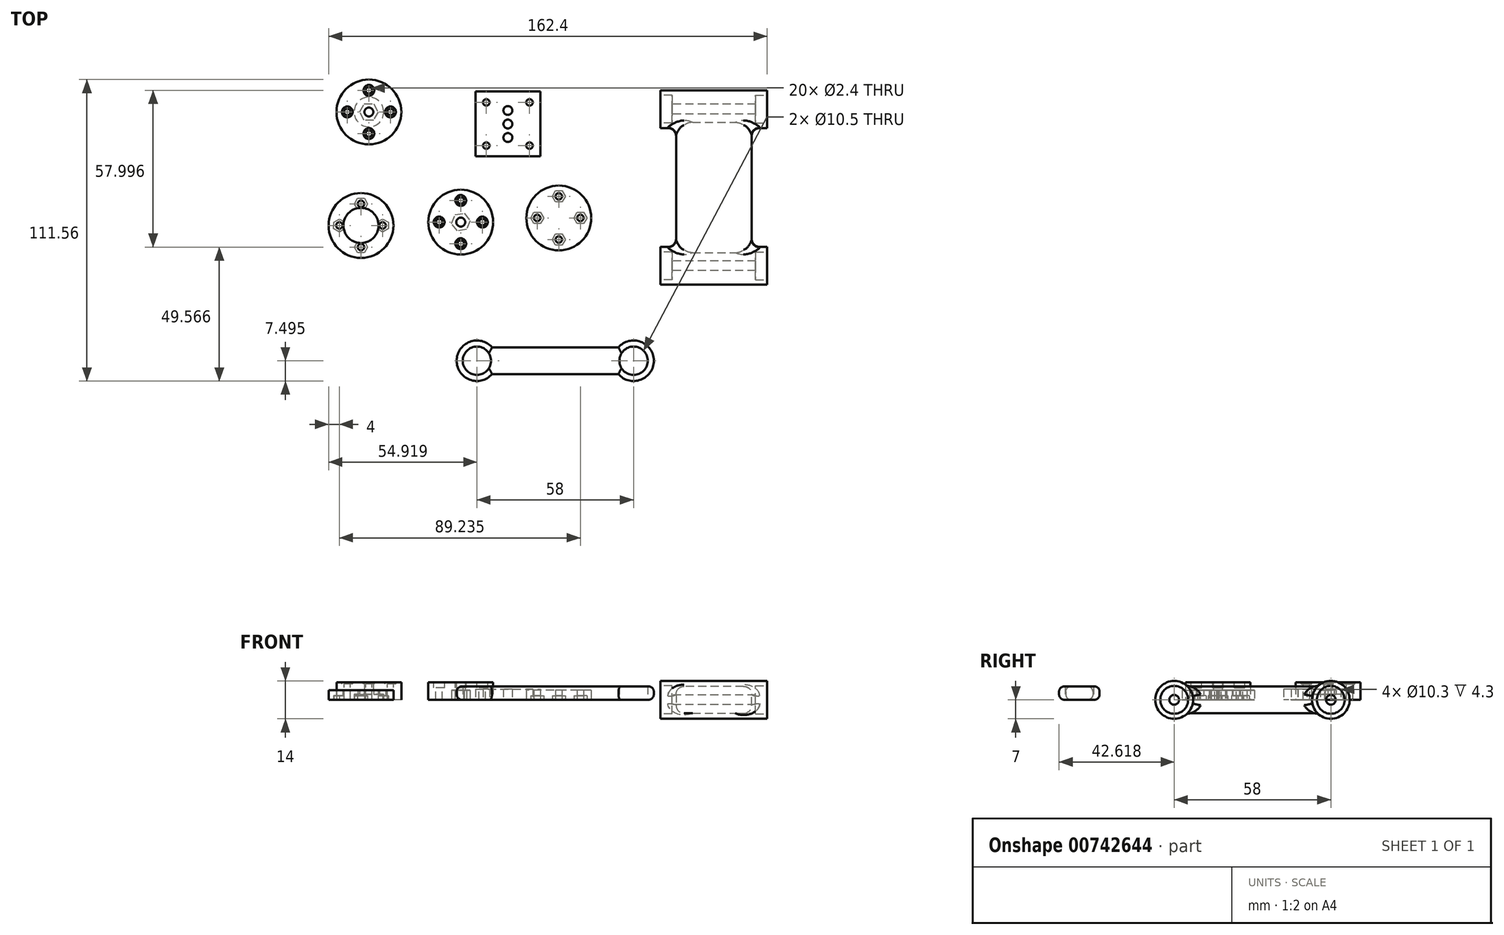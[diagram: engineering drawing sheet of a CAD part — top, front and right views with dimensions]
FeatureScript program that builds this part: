
annotation { "Feature Type Name" : "Feature", "Feature Type Description" : "" }
export const myFeature = defineFeature(function(context is Context, id is Id, definition is map)
    precondition{}
    {
        {
            var Q0;
            Q0=qCreatedBy(makeId("Top.planeOp"),FACE);
            var sketch = newSketch(context, id + "F0", { "sketchPlane" : qUnion([Q0])});
            skLineSegment(sketch, "E0.bottom", {"start": v(-51.58, 38.28) * mm, "end": v(-35.58, 38.28) * mm, "construction": true});
            skLineSegment(sketch, "E0.top", {"start": v(-51.58, 22.28) * mm, "end": v(-35.58, 22.28) * mm, "construction": true});
            skLineSegment(sketch, "E0.left", {"start": v(-51.58, 38.28) * mm, "end": v(-51.58, 22.28) * mm, "construction": true});
            skLineSegment(sketch, "E0.right", {"start": v(-35.58, 38.28) * mm, "end": v(-35.58, 22.28) * mm, "construction": true});
            skLineSegment(sketch, "E1.bottom", {"start": v(-55.58, 42.28) * mm, "end": v(-31.58, 42.28) * mm});
            skLineSegment(sketch, "E1.top", {"start": v(-55.58, 18.28) * mm, "end": v(-31.58, 18.28) * mm});
            skLineSegment(sketch, "E1.left", {"start": v(-55.58, 42.28) * mm, "end": v(-55.58, 18.28) * mm});
            skLineSegment(sketch, "E1.right", {"start": v(-31.58, 42.28) * mm, "end": v(-31.58, 18.28) * mm});
            skPoint(sketch, "E1.middle", {"position": v(-43.58, 30.28) * mm});
            skPoint(sketch, "E1.middle.positionSnap1", {"position": v(-35.58, 30.28) * mm});
            skPoint(sketch, "E1.centerSnap0", {"position": v(-43.58, 38.28) * mm});
            skPoint(sketch, "E1.centerSnap1", {"position": v(-35.58, 30.28) * mm});
            skPoint(sketch, "E2", {"position": v(-43.58, 22.28) * mm});
            skPoint(sketch, "E3", {"position": v(-43.58, 35.28) * mm});
            skPoint(sketch, "E4", {"position": v(-43.58, 25.28) * mm});
            skLineSegment(sketch, "E5", {"start": v(-43.58, 38.28) * mm, "end": v(-43.58, 35.28) * mm, "construction": true});
            skLineSegment(sketch, "E6", {"start": v(-43.58, 25.28) * mm, "end": v(-43.58, 22.28) * mm, "construction": true});
            skCircle(sketch, "E7", {"center": v(-35.58, 38.28) * mm, "radius": 0.75 * mm});
            skCircle(sketch, "E8", {"center": v(-51.58, 38.28) * mm, "radius": 0.75 * mm});
            skCircle(sketch, "E9", {"center": v(-51.58, 22.28) * mm, "radius": 0.75 * mm});
            skCircle(sketch, "E10", {"center": v(-35.58, 22.28) * mm, "radius": 0.75 * mm});
            skSolve(sketch);
        }
        {
            var Q0;
            Q0=makeQuery(id+"F0.imprint","IMPRINT",FACE,{"disambiguationData":[TD([[makeQuery(id+"F0.imprint","IMPRINT",EDGE,{"derivedFrom":sQuery(id+"F0.wireOp",EDGE,"E1.bottom")}),-1.0]])]});
            var Q1;
            Q1=makeQuery(id+"F0.imprint","IMPRINT",FACE,{"disambiguationData":[TD([[makeQuery(id+"F0.imprint","IMPRINT",EDGE,{"derivedFrom":sQuery(id+"F0.wireOp",EDGE,"E7")}),1.0]])]});
            var Q2;
            Q2=makeQuery(id+"F0.imprint","IMPRINT",FACE,{"disambiguationData":[TD([[makeQuery(id+"F0.imprint","IMPRINT",EDGE,{"derivedFrom":sQuery(id+"F0.wireOp",EDGE,"E8")}),1.0]])]});
            var Q3;
            Q3=makeQuery(id+"F0.imprint","IMPRINT",FACE,{"disambiguationData":[TD([[makeQuery(id+"F0.imprint","IMPRINT",EDGE,{"derivedFrom":sQuery(id+"F0.wireOp",EDGE,"E9")}),1.0]])]});
            var Q4;
            Q4=makeQuery(id+"F0.imprint","IMPRINT",FACE,{"disambiguationData":[TD([[makeQuery(id+"F0.imprint","IMPRINT",EDGE,{"derivedFrom":sQuery(id+"F0.wireOp",EDGE,"E10")}),1.0]])]});
            extrude(context, id + "F1", {"entities" : qUnion([Q0, Q1, Q2, Q3, Q4]), "depth" : 4 * mm, "offsetDistance" : 25 * mm});
        }
        {
            var Q0;
            Q0=sQuery(id+"F0.wireOp",VERTEX,"E1.middle.positionSnap0");
            var Q1;
            Q1=sQuery(id+"F0.wireOp",VERTEX,"455f30e0-36e8-462a-b0a7-f685abfa277a");
            var Q2;
            Q2=sQuery(id+"F0.wireOp",VERTEX,"E1.middle");
            var Q3;
            Q3=sQuery(id+"F0.wireOp",VERTEX,"a96c1f38-2630-4629-b729-bfcacf4a2e01");
            var Q4;
            Q4=sQuery(id+"F0.wireOp",VERTEX,"E3");
            var Q5;
            Q5=sQuery(id+"F0.wireOp",VERTEX,"E4");
            var Q6;
            Q6=makeQuery(id+"F1.opExtrude","SWEPT_BODY",BODY,{"disambiguationData":[OSD([sQuery(id+"F0.wireOp",EDGE,"E1.bottom"),sQuery(id+"F0.wireOp",EDGE,"E1.top"),sQuery(id+"F0.wireOp",EDGE,"E1.left"),sQuery(id+"F0.wireOp",EDGE,"E1.right")])]});
            hole(context, id + "F2", {"style" : HoleStyle.SIMPLE, "endStyle" : HoleEndStyle.BLIND, "oppositeDirection" : true, "holeDiameter" : 3.3 * mm, "majorDiameter" : 5 * mm, "holeDepth" : 12 * mm, "isTappedThrough" : true, "tappedDepth" : 10.5 * mm, "tapClearance" : 3, "locations" : qUnion([Q0, Q1, Q2, Q3, Q4, Q5]), "scope" : qUnion([Q6])});
        }
        {
            var Q0;
            Q0=sQuery(id+"F0.wireOp",VERTEX,"E0.top.start");
            var Q1;
            Q1=sQuery(id+"F0.wireOp",VERTEX,"E0.top.end");
            var Q2;
            Q2=sQuery(id+"F0.wireOp",VERTEX,"E0.bottom.end");
            var Q3;
            Q3=sQuery(id+"F0.wireOp",VERTEX,"E0.bottom.start");
            var Q4;
            Q4=makeQuery(id+"F1.opExtrude","SWEPT_BODY",BODY,{"disambiguationData":[OSD([sQuery(id+"F0.wireOp",EDGE,"E1.bottom"),sQuery(id+"F0.wireOp",EDGE,"E1.top"),sQuery(id+"F0.wireOp",EDGE,"E1.left"),sQuery(id+"F0.wireOp",EDGE,"E1.right")])]});
            hole(context, id + "F3", {"style" : HoleStyle.SIMPLE, "endStyle" : HoleEndStyle.BLIND, "oppositeDirection" : true, "holeDiameter" : 2.4 * mm, "majorDiameter" : 5 * mm, "holeDepth" : 30 * mm, "isTappedThrough" : true, "tappedDepth" : 10.5 * mm, "tapClearance" : 3, "locations" : qUnion([Q0, Q1, Q2, Q3]), "scope" : qUnion([Q4])});
        }
        {
            var Q0;
            Q0=qCreatedBy(makeId("Top.planeOp"),FACE);
            var sketch = newSketch(context, id + "F4", { "sketchPlane" : qUnion([Q0])});
            skLineSegment(sketch, "E11", {"start": v(12.93, 35.79) * mm, "end": v(52.43, 35.79) * mm});
            skLineSegment(sketch, "E12", {"start": v(32.68, 35.79) * mm, "end": v(32.68, -22.21) * mm});
            skLineSegment(sketch, "E13", {"start": v(13, -22.21) * mm, "end": v(52.5, -22.21) * mm});
            skSolve(sketch);
        }
        {
            var Q0;
            Q0=qCreatedBy(makeId("Right.planeOp"),FACE);
            var Q1;
            Q1=sQuery(id+"F4.wireOp",VERTEX,"E11.start");
            cPlane(context, id + "F5", {"entities" : qUnion([Q0, Q1]), "cplaneType" : CPlaneType.PLANE_POINT, "offset" : 25 * mm, "width" : 150 * mm, "height" : 150 * mm});
        }
        {
            var Q0;
            Q0=qCreatedBy(id+"F5.planeOp",FACE);
            var sketch = newSketch(context, id + "F6", { "sketchPlane" : qUnion([Q0])});
            skCircle(sketch, "E14", {"center": v(35.79, 0) * mm, "radius": 7 * mm});
            skCircle(sketch, "E15", {"center": v(-22.21, 0) * mm, "radius": 7 * mm});
            skCircle(sketch, "E16", {"center": v(35.79, 0) * mm, "radius": 5.15 * mm});
            skCircle(sketch, "E17", {"center": v(-22.21, 0) * mm, "radius": 5.15 * mm});
            skSolve(sketch);
        }
        {
            var Q0;
            Q0=sQuery(id+"F4.wireOp",EDGE,"E13");
            cPoint(context, id + "F7", {"entities" : qUnion([Q0]), "parameter" : 0.5});
        }
        {
            var Q0;
            Q0=qCreatedBy(makeId("Front.planeOp"),FACE);
            var Q1;
            Q1 = qCreatedBy(id + "F7" ,VERTEX);
            cPlane(context, id + "F8", {"entities" : qUnion([Q0, Q1]), "cplaneType" : CPlaneType.PLANE_POINT, "offset" : 25 * mm, "width" : 150 * mm, "height" : 150 * mm});
        }
        {
            var Q0;
            Q0=qCreatedBy(id+"F8.planeOp",FACE);
            var sketch = newSketch(context, id + "F9", { "sketchPlane" : qUnion([Q0])});
            skLineSegment(sketch, "E18.bottom", {"start": v(46.68, 5) * mm, "end": v(18.68, 5) * mm});
            skLineSegment(sketch, "E18.top", {"start": v(46.68, -5) * mm, "end": v(18.68, -5) * mm});
            skLineSegment(sketch, "E18.left", {"start": v(46.68, 5) * mm, "end": v(46.68, -5) * mm});
            skLineSegment(sketch, "E18.right", {"start": v(18.68, 5) * mm, "end": v(18.68, -5) * mm});
            skPoint(sketch, "E18.middle", {"position": v(32.68, 0) * mm});
            skSolve(sketch);
        }
        {
            var Q0;
            Q0=makeQuery(id+"F6.imprint","IMPRINT",FACE,{"disambiguationData":[TD([[makeQuery(id+"F6.imprint","IMPRINT",EDGE,{"derivedFrom":sQuery(id+"F6.wireOp",EDGE,"E14")}),1.0]])]});
            var Q1;
            Q1=makeQuery(id+"F6.imprint","IMPRINT",FACE,{"disambiguationData":[TD([[makeQuery(id+"F6.imprint","IMPRINT",EDGE,{"derivedFrom":sQuery(id+"F6.wireOp",EDGE,"E15")}),1.0]])]});
            var Q2;
            Q2=makeQuery(id+"F6.imprint","IMPRINT",FACE,{"disambiguationData":[TD([[makeQuery(id+"F6.imprint","IMPRINT",EDGE,{"derivedFrom":sQuery(id+"F6.wireOp",EDGE,"E16")}),1.0]])]});
            var Q3;
            Q3=makeQuery(id+"F6.imprint","IMPRINT",FACE,{"disambiguationData":[TD([[makeQuery(id+"F6.imprint","IMPRINT",EDGE,{"derivedFrom":sQuery(id+"F6.wireOp",EDGE,"E17")}),1.0]])]});
            var Q4;
            Q4=sQuery(id+"F6.wireOp",EDGE,"E14");
            var Q5;
            Q5=sQuery(id+"F6.wireOp",EDGE,"E15");
            var Q6;
            Q6=sQuery(id+"F4.wireOp",EDGE,"E11");
            sweep(context, id + "F10", {"profiles" : qUnion([Q0, Q1, Q2, Q3]), "surfaceProfiles" : qUnion([Q4, Q5]), "path" : qUnion([Q6])});
        }
        {
            var Q0;
            Q0=makeQuery(id+"F9.imprint","IMPRINT",FACE,{"disambiguationData":[TD([[makeQuery(id+"F9.imprint","IMPRINT",EDGE,{"derivedFrom":sQuery(id+"F9.wireOp",EDGE,"E18.bottom")}),1.0]])]});
            var Q1;
            Q1=sQuery(id+"F4.wireOp",EDGE,"E12");
            sweep(context, id + "F11", {"operationType" : NewBodyOperationType.ADD, "profiles" : qUnion([Q0]), "path" : qUnion([Q1])});
        }
        {
            var Q0;
            Q0=makeQuery(id+"F11.opSweep","SWEPT_FACE",FACE,{"disambiguationData":[OSD([sQuery(id+"F4.wireOp",EDGE,"E12"),sQuery(id+"F9.wireOp",EDGE,"E18.right")])]});
            var Q1;
            Q1=makeQuery(id+"F11.opSweep","SWEPT_FACE",FACE,{"disambiguationData":[OSD([sQuery(id+"F4.wireOp",EDGE,"E12"),sQuery(id+"F9.wireOp",EDGE,"E18.left")])]});
            var Q2;
            Q2=makeQuery(id+"F11.opSweep","SWEPT_FACE",FACE,{"disambiguationData":[OSD([sQuery(id+"F4.wireOp",EDGE,"E12"),sQuery(id+"F9.wireOp",EDGE,"E18.bottom")])]});
            fillet(context, id + "F12", {"entities" : qUnion([Q0, Q1, Q2]), "radius" : 3 * mm, "tangentPropagation" : true, "allowEdgeOverflow" : false});
        }
        {
            var Q0;
            Q0=sQuery(id+"F6.wireOp",VERTEX,"E14.center");
            var Q1;
            Q1=sQuery(id+"F6.wireOp",VERTEX,"E15.center");
            var Q2;
            Q2=makeQuery(id+"F10.opSweep","SWEPT_BODY",BODY,{"disambiguationData":[OSD([sQuery(id+"F4.wireOp",EDGE,"E11"),sQuery(id+"F6.wireOp",EDGE,"E14")])]});
            hole(context, id + "F13", {"style" : HoleStyle.SIMPLE, "endStyle" : HoleEndStyle.THROUGH, "oppositeDirection" : true, "holeDiameter" : 3.6 * mm, "majorDiameter" : 5 * mm, "isTappedThrough" : true, "tappedDepth" : 10.5 * mm, "tapClearance" : 3, "locations" : qUnion([Q0, Q1]), "scope" : qUnion([Q2])});
        }
        {
            var Q0;
            Q0=makeQuery(id+"F10.opSweep","CAP_FACE",FACE,{"disambiguationData":[OSD([sQuery(id+"F4.wireOp",VERTEX,"E11.end"),sQuery(id+"F6.wireOp",EDGE,"E14")])],"isStart":false});
            var sketch = newSketch(context, id + "F14", { "sketchPlane" : qUnion([Q0])});
            skCircle(sketch, "E19", {"center": v(-22.21, 0) * mm, "radius": 5.15 * mm});
            skCircle(sketch, "E20", {"center": v(35.79, 0) * mm, "radius": 5.15 * mm});
            skSolve(sketch);
        }
        {
            var Q0;
            Q0=makeQuery(id+"F14.imprint","IMPRINT",FACE,{"disambiguationData":[TD([[makeQuery(id+"F14.imprint","IMPRINT",EDGE,{"derivedFrom":sQuery(id+"F14.wireOp",EDGE,"E19")}),1.0]])]});
            var Q1;
            Q1=makeQuery(id+"F6.imprint","IMPRINT",FACE,{"disambiguationData":[TD([[makeQuery(id+"F6.imprint","IMPRINT",EDGE,{"derivedFrom":sQuery(id+"F6.wireOp",EDGE,"E17")}),1.0]])]});
            var Q2;
            Q2=makeQuery(id+"F14.imprint","IMPRINT",FACE,{"disambiguationData":[TD([[makeQuery(id+"F14.imprint","IMPRINT",EDGE,{"derivedFrom":sQuery(id+"F14.wireOp",EDGE,"E20")}),1.0]])]});
            extrude(context, id + "F15", {"entities" : qUnion([Q0, Q1, Q2]), "operationType" : NewBodyOperationType.REMOVE, "oppositeDirection" : true, "depth" : 4.3 * mm, "offsetDistance" : 25 * mm});
        }
        {
            var Q0;
            Q0=makeQuery(id+"F6.imprint","IMPRINT",FACE,{"disambiguationData":[TD([[makeQuery(id+"F6.imprint","IMPRINT",EDGE,{"derivedFrom":sQuery(id+"F6.wireOp",EDGE,"E17")}),1.0]])]});
            var Q1;
            Q1=makeQuery(id+"F6.imprint","IMPRINT",FACE,{"disambiguationData":[TD([[makeQuery(id+"F6.imprint","IMPRINT",EDGE,{"derivedFrom":sQuery(id+"F6.wireOp",EDGE,"E16")}),1.0]])]});
            extrude(context, id + "F16", {"entities" : qUnion([Q0, Q1]), "operationType" : NewBodyOperationType.REMOVE, "depth" : 4.3 * mm, "offsetDistance" : 25 * mm});
        }
        {
            var Q0;
            Q0=qCreatedBy(makeId("Top.planeOp"),FACE);
            var sketch = newSketch(context, id + "F17", { "sketchPlane" : qUnion([Q0])});
            skCircle(sketch, "E21", {"center": v(-61.03, -6.02) * mm, "radius": 8 * mm, "construction": true});
            skCircle(sketch, "E22", {"center": v(-61.03, -6.02) * mm, "radius": 12 * mm});
            skPoint(sketch, "E23", {"position": v(-61.03, 1.98) * mm});
            skPoint(sketch, "E24", {"position": v(-61.03, -14.02) * mm});
            skPoint(sketch, "E25", {"position": v(-53.03, -6.02) * mm});
            skPoint(sketch, "E26", {"position": v(-69.03, -6.02) * mm});
            skCircle(sketch, "E27.cCircle", {"center": v(-61.03, -6.02) * mm, "radius": 3 * mm, "construction": true});
            skLineSegment(sketch, "E27.0", {"start": v(-59.75, -2.8) * mm, "end": v(-57.6, -5.52) * mm});
            skLineSegment(sketch, "E27.1", {"start": v(-57.6, -5.52) * mm, "end": v(-58.89, -8.74) * mm});
            skLineSegment(sketch, "E27.2", {"start": v(-58.89, -8.74) * mm, "end": v(-62.32, -9.24) * mm});
            skLineSegment(sketch, "E27.3", {"start": v(-62.32, -9.24) * mm, "end": v(-64.46, -6.52) * mm});
            skLineSegment(sketch, "E27.4", {"start": v(-64.46, -6.52) * mm, "end": v(-63.18, -3.3) * mm});
            skLineSegment(sketch, "E27.5", {"start": v(-63.18, -3.3) * mm, "end": v(-59.75, -2.8) * mm});
            skPoint(sketch, "E27.0.midPoint", {"position": v(-58.68, -4.16) * mm});
            skCircle(sketch, "E28", {"center": v(-24.74, -4.5) * mm, "radius": 8 * mm, "construction": true});
            skCircle(sketch, "E29", {"center": v(-24.74, -4.5) * mm, "radius": 12 * mm});
            skPoint(sketch, "E30", {"position": v(-24.74, -12.5) * mm});
            skPoint(sketch, "E31", {"position": v(-16.74, -4.5) * mm});
            skPoint(sketch, "E32", {"position": v(-32.74, -4.5) * mm});
            skPoint(sketch, "E33", {"position": v(-24.74, 3.5) * mm});
            skCircle(sketch, "E34.cCircle", {"center": v(-24.74, 3.5) * mm, "radius": 2.1 * mm, "construction": true});
            skLineSegment(sketch, "E34.0", {"start": v(-23.52, 5.6) * mm, "end": v(-22.31, 3.5) * mm});
            skLineSegment(sketch, "E34.1", {"start": v(-22.31, 3.5) * mm, "end": v(-23.52, 1.4) * mm});
            skLineSegment(sketch, "E34.2", {"start": v(-23.52, 1.4) * mm, "end": v(-25.95, 1.4) * mm});
            skLineSegment(sketch, "E34.3", {"start": v(-25.95, 1.4) * mm, "end": v(-27.16, 3.5) * mm});
            skLineSegment(sketch, "E34.4", {"start": v(-27.16, 3.5) * mm, "end": v(-25.95, 5.6) * mm});
            skLineSegment(sketch, "E34.5", {"start": v(-25.95, 5.6) * mm, "end": v(-23.52, 5.6) * mm});
            skPoint(sketch, "E34.0.midPoint", {"position": v(-22.92, 4.56) * mm});
            skCircle(sketch, "E35.cCircle", {"center": v(-16.74, -4.5) * mm, "radius": 2.1 * mm, "construction": true});
            skLineSegment(sketch, "E35.0", {"start": v(-17.95, -2.4) * mm, "end": v(-15.52, -2.4) * mm});
            skLineSegment(sketch, "E35.1", {"start": v(-15.52, -2.4) * mm, "end": v(-14.31, -4.5) * mm});
            skLineSegment(sketch, "E35.2", {"start": v(-14.31, -4.5) * mm, "end": v(-15.52, -6.6) * mm});
            skLineSegment(sketch, "E35.3", {"start": v(-15.52, -6.6) * mm, "end": v(-17.95, -6.6) * mm});
            skLineSegment(sketch, "E35.4", {"start": v(-17.95, -6.6) * mm, "end": v(-19.16, -4.5) * mm});
            skLineSegment(sketch, "E35.5", {"start": v(-19.16, -4.5) * mm, "end": v(-17.95, -2.4) * mm});
            skPoint(sketch, "E35.0.midPoint", {"position": v(-16.74, -2.4) * mm});
            skCircle(sketch, "E36.cCircle", {"center": v(-24.74, -12.5) * mm, "radius": 2.1 * mm, "construction": true});
            skLineSegment(sketch, "E36.0", {"start": v(-23.52, -10.4) * mm, "end": v(-22.31, -12.5) * mm});
            skLineSegment(sketch, "E36.1", {"start": v(-22.31, -12.5) * mm, "end": v(-23.52, -14.6) * mm});
            skLineSegment(sketch, "E36.2", {"start": v(-23.52, -14.6) * mm, "end": v(-25.95, -14.6) * mm});
            skLineSegment(sketch, "E36.3", {"start": v(-25.95, -14.6) * mm, "end": v(-27.16, -12.5) * mm});
            skLineSegment(sketch, "E36.4", {"start": v(-27.16, -12.5) * mm, "end": v(-25.95, -10.4) * mm});
            skLineSegment(sketch, "E36.5", {"start": v(-25.95, -10.4) * mm, "end": v(-23.52, -10.4) * mm});
            skPoint(sketch, "E36.0.midPoint", {"position": v(-22.92, -11.44) * mm});
            skCircle(sketch, "E37.cCircle", {"center": v(-32.74, -4.5) * mm, "radius": 2.1 * mm, "construction": true});
            skLineSegment(sketch, "E37.0", {"start": v(-31.52, -2.4) * mm, "end": v(-30.31, -4.5) * mm});
            skLineSegment(sketch, "E37.1", {"start": v(-30.31, -4.5) * mm, "end": v(-31.52, -6.6) * mm});
            skLineSegment(sketch, "E37.2", {"start": v(-31.52, -6.6) * mm, "end": v(-33.95, -6.6) * mm});
            skLineSegment(sketch, "E37.3", {"start": v(-33.95, -6.6) * mm, "end": v(-35.16, -4.5) * mm});
            skLineSegment(sketch, "E37.4", {"start": v(-35.16, -4.5) * mm, "end": v(-33.95, -2.4) * mm});
            skLineSegment(sketch, "E37.5", {"start": v(-33.95, -2.4) * mm, "end": v(-31.52, -2.4) * mm});
            skPoint(sketch, "E37.0.midPoint", {"position": v(-30.92, -3.44) * mm});
            skLineSegment(sketch, "E38", {"start": v(-36.74, -4.5) * mm, "end": v(-12.74, -4.5) * mm, "construction": true});
            skLineSegment(sketch, "E39", {"start": v(-24.74, 7.5) * mm, "end": v(-24.74, -16.5) * mm, "construction": true});
            skPoint(sketch, "E40", {"position": v(-24.74, 5.6) * mm});
            skPoint(sketch, "E41", {"position": v(-24.74, -10.4) * mm});
            skCircle(sketch, "E42", {"center": v(-55.05, -57.33) * mm, "radius": 5.25 * mm});
            skCircle(sketch, "E43", {"center": v(-55.05, -57.33) * mm, "radius": 7.5 * mm});
            skLineSegment(sketch, "E44", {"start": v(-55.05, -57.33) * mm, "end": v(2.95, -57.33) * mm});
            skCircle(sketch, "E45", {"center": v(2.95, -57.33) * mm, "radius": 5.25 * mm});
            skCircle(sketch, "E46", {"center": v(2.95, -57.33) * mm, "radius": 7.5 * mm});
            skPoint(sketch, "E47", {"position": v(-26.05, -57.33) * mm});
            skLineSegment(sketch, "E48.bottom", {"start": v(-49.46, -52.33) * mm, "end": v(-2.64, -52.33) * mm});
            skLineSegment(sketch, "E48.top", {"start": v(-49.46, -62.33) * mm, "end": v(-2.64, -62.33) * mm});
            skLineSegment(sketch, "E48.left", {"start": v(-49.46, -52.33) * mm, "end": v(-49.46, -62.33) * mm});
            skLineSegment(sketch, "E48.right", {"start": v(-2.64, -52.33) * mm, "end": v(-2.64, -62.33) * mm});
            skCircle(sketch, "E49", {"center": v(-97.97, -7.26) * mm, "radius": 8 * mm, "construction": true});
            skCircle(sketch, "E50", {"center": v(-97.97, -7.26) * mm, "radius": 12 * mm});
            skPoint(sketch, "E51", {"position": v(-97.97, -15.26) * mm});
            skPoint(sketch, "E52", {"position": v(-89.97, -7.26) * mm});
            skPoint(sketch, "E53", {"position": v(-105.97, -7.26) * mm});
            skPoint(sketch, "E54", {"position": v(-97.97, 0.74) * mm});
            skCircle(sketch, "E55.cCircle", {"center": v(-97.97, 0.74) * mm, "radius": 2.1 * mm, "construction": true});
            skLineSegment(sketch, "E55.0", {"start": v(-96.76, 2.84) * mm, "end": v(-95.55, 0.74) * mm});
            skLineSegment(sketch, "E55.1", {"start": v(-95.55, 0.74) * mm, "end": v(-96.76, -1.36) * mm});
            skLineSegment(sketch, "E55.2", {"start": v(-96.76, -1.36) * mm, "end": v(-99.18, -1.36) * mm});
            skLineSegment(sketch, "E55.3", {"start": v(-99.18, -1.36) * mm, "end": v(-100.4, 0.74) * mm});
            skLineSegment(sketch, "E55.4", {"start": v(-100.4, 0.74) * mm, "end": v(-99.18, 2.84) * mm});
            skLineSegment(sketch, "E55.5", {"start": v(-99.18, 2.84) * mm, "end": v(-96.76, 2.84) * mm});
            skPoint(sketch, "E55.0.midPoint", {"position": v(-96.15, 1.79) * mm});
            skCircle(sketch, "E56.cCircle", {"center": v(-97.97, -15.26) * mm, "radius": 2.1 * mm, "construction": true});
            skLineSegment(sketch, "E56.0", {"start": v(-96.76, -13.16) * mm, "end": v(-95.55, -15.26) * mm});
            skLineSegment(sketch, "E56.1", {"start": v(-95.55, -15.26) * mm, "end": v(-96.76, -17.36) * mm});
            skLineSegment(sketch, "E56.2", {"start": v(-96.76, -17.36) * mm, "end": v(-99.18, -17.36) * mm});
            skLineSegment(sketch, "E56.3", {"start": v(-99.18, -17.36) * mm, "end": v(-100.4, -15.26) * mm});
            skLineSegment(sketch, "E56.4", {"start": v(-100.4, -15.26) * mm, "end": v(-99.18, -13.16) * mm});
            skLineSegment(sketch, "E56.5", {"start": v(-99.18, -13.16) * mm, "end": v(-96.76, -13.16) * mm});
            skPoint(sketch, "E56.0.midPoint", {"position": v(-96.15, -14.21) * mm});
            skLineSegment(sketch, "E57", {"start": v(-109.97, -7.26) * mm, "end": v(-85.97, -7.26) * mm, "construction": true});
            skLineSegment(sketch, "E58", {"start": v(-97.97, 4.74) * mm, "end": v(-97.97, -19.26) * mm, "construction": true});
            skPoint(sketch, "E59", {"position": v(-97.97, 2.84) * mm});
            skPoint(sketch, "E60", {"position": v(-97.97, -13.16) * mm});
            skCircle(sketch, "E61", {"center": v(-97.97, -7.26) * mm, "radius": 6.5 * mm});
            skLineSegment(sketch, "E62", {"start": v(-89.97, 0.12) * mm, "end": v(-89.97, -14.94) * mm, "construction": true});
            skLineSegment(sketch, "E63", {"start": v(-105.97, -0.94) * mm, "end": v(-105.97, -14.47) * mm, "construction": true});
            skCircle(sketch, "E64.cCircle", {"center": v(-105.97, -7.26) * mm, "radius": 2.1 * mm, "construction": true});
            skLineSegment(sketch, "E64.0", {"start": v(-108.05, -6.02) * mm, "end": v(-105.94, -4.84) * mm});
            skLineSegment(sketch, "E64.1", {"start": v(-105.94, -4.84) * mm, "end": v(-103.85, -6.08) * mm});
            skLineSegment(sketch, "E64.2", {"start": v(-103.85, -6.08) * mm, "end": v(-103.89, -8.5) * mm});
            skLineSegment(sketch, "E64.3", {"start": v(-103.89, -8.5) * mm, "end": v(-106, -9.69) * mm});
            skLineSegment(sketch, "E64.4", {"start": v(-106, -9.69) * mm, "end": v(-108.09, -8.45) * mm});
            skLineSegment(sketch, "E64.5", {"start": v(-108.09, -8.45) * mm, "end": v(-108.05, -6.02) * mm});
            skPoint(sketch, "E64.0.midPoint", {"position": v(-107, -5.43) * mm});
            skCircle(sketch, "E65.cCircle", {"center": v(-89.97, -7.26) * mm, "radius": 2.1 * mm, "construction": true});
            skLineSegment(sketch, "E65.0", {"start": v(-89.97, -4.84) * mm, "end": v(-87.87, -6.05) * mm});
            skLineSegment(sketch, "E65.1", {"start": v(-87.87, -6.05) * mm, "end": v(-87.87, -8.48) * mm});
            skLineSegment(sketch, "E65.2", {"start": v(-87.87, -8.48) * mm, "end": v(-89.97, -9.69) * mm});
            skLineSegment(sketch, "E65.3", {"start": v(-89.97, -9.69) * mm, "end": v(-92.07, -8.48) * mm});
            skLineSegment(sketch, "E65.4", {"start": v(-92.07, -8.48) * mm, "end": v(-92.07, -6.05) * mm});
            skLineSegment(sketch, "E65.5", {"start": v(-92.07, -6.05) * mm, "end": v(-89.97, -4.84) * mm});
            skPoint(sketch, "E65.0.midPoint", {"position": v(-88.92, -5.45) * mm});
            skCircle(sketch, "E66", {"center": v(-95.05, 34.73) * mm, "radius": 8 * mm, "construction": true});
            skCircle(sketch, "E67", {"center": v(-95.05, 34.73) * mm, "radius": 12 * mm});
            skPoint(sketch, "E68", {"position": v(-95.05, 42.73) * mm});
            skPoint(sketch, "E69", {"position": v(-95.05, 26.73) * mm});
            skPoint(sketch, "E70", {"position": v(-87.05, 34.73) * mm});
            skPoint(sketch, "E71", {"position": v(-103.05, 34.73) * mm});
            skCircle(sketch, "E72.cCircle", {"center": v(-95.05, 34.73) * mm, "radius": 3 * mm, "construction": true});
            skLineSegment(sketch, "E72.0", {"start": v(-93.32, 37.73) * mm, "end": v(-91.59, 34.73) * mm});
            skLineSegment(sketch, "E72.1", {"start": v(-91.59, 34.73) * mm, "end": v(-93.32, 31.73) * mm});
            skLineSegment(sketch, "E72.2", {"start": v(-93.32, 31.73) * mm, "end": v(-96.78, 31.73) * mm});
            skLineSegment(sketch, "E72.3", {"start": v(-96.78, 31.73) * mm, "end": v(-98.51, 34.73) * mm});
            skLineSegment(sketch, "E72.4", {"start": v(-98.51, 34.73) * mm, "end": v(-96.78, 37.73) * mm});
            skLineSegment(sketch, "E72.5", {"start": v(-96.78, 37.73) * mm, "end": v(-93.32, 37.73) * mm});
            skPoint(sketch, "E72.0.midPoint", {"position": v(-92.45, 36.23) * mm});
            skCircle(sketch, "E73", {"center": v(-95.05, 34.73) * mm, "radius": 5.5 * mm});
            skLineSegment(sketch, "E74", {"start": v(-95.05, 46.73) * mm, "end": v(-95.05, 22.73) * mm, "construction": true});
            skLineSegment(sketch, "E75", {"start": v(-107.05, 34.73) * mm, "end": v(-83.05, 34.73) * mm, "construction": true});
            skSolve(sketch);
        }
        {
            var Q0;
            Q0=makeQuery(id+"F17.imprint","IMPRINT",FACE,{"disambiguationData":[TD([[makeQuery(id+"F17.imprint","IMPRINT",EDGE,{"derivedFrom":sQuery(id+"F17.wireOp",EDGE,"E22")}),1.0]])]});
            var Q1;
            Q1=makeQuery(id+"F17.imprint","IMPRINT",FACE,{"disambiguationData":[TD([[makeQuery(id+"F17.imprint","IMPRINT",EDGE,{"derivedFrom":sQuery(id+"F17.wireOp",EDGE,"E27.0")}),-1.0]])]});
            var Q2;
            Q2=makeQuery(id+"F17.imprint","IMPRINT",FACE,{"disambiguationData":[TD([[makeQuery(id+"F17.imprint","IMPRINT",EDGE,{"derivedFrom":sQuery(id+"F17.wireOp",EDGE,"E67")}),1.0]])]});
            var Q3;
            Q3=makeQuery(id+"F17.imprint","IMPRINT",FACE,{"disambiguationData":[TD([[makeQuery(id+"F17.imprint","IMPRINT",EDGE,{"derivedFrom":sQuery(id+"F17.wireOp",EDGE,"E72.0")}),1.0]])]});
            var Q4;
            Q4=makeQuery(id+"F17.imprint","IMPRINT",FACE,{"disambiguationData":[TD([[makeQuery(id+"F17.imprint","IMPRINT",EDGE,{"derivedFrom":sQuery(id+"F17.wireOp",EDGE,"E72.0")}),-1.0]])]});
            extrude(context, id + "F18", {"entities" : qUnion([Q0, Q1, Q2, Q3, Q4]), "depth" : 6.5 * mm, "offsetDistance" : 25 * mm});
        }
        {
            var Q0;
            Q0=makeQuery(id+"F17.imprint","IMPRINT",FACE,{"disambiguationData":[TD([[makeQuery(id+"F17.imprint","IMPRINT",EDGE,{"derivedFrom":sQuery(id+"F17.wireOp",EDGE,"E27.0")}),-1.0]])]});
            var Q1;
            Q1=makeQuery(id+"F17.imprint","IMPRINT",FACE,{"disambiguationData":[TD([[makeQuery(id+"F17.imprint","IMPRINT",EDGE,{"derivedFrom":sQuery(id+"F17.wireOp",EDGE,"E72.0")}),-1.0]])]});
            extrude(context, id + "F19", {"entities" : qUnion([Q0, Q1]), "operationType" : NewBodyOperationType.REMOVE, "depth" : 3.5 * mm, "offsetDistance" : 25 * mm});
        }
        {
            var Q0;
            Q0=sQuery(id+"F17.wireOp",VERTEX,"E21.center");
            var Q1;
            Q1=sQuery(id+"F17.wireOp",VERTEX,"E66.center");
            var Q2;
            Q2=makeQuery(id+"F18.opExtrude","SWEPT_BODY",BODY,{"disambiguationData":[OSD([sQuery(id+"F17.wireOp",EDGE,"E22")])]});
            var Q3;
            Q3=makeQuery(id+"F18.opExtrude","SWEPT_BODY",BODY,{"disambiguationData":[OSD([sQuery(id+"F17.wireOp",EDGE,"E67")])]});
            hole(context, id + "F20", {"style" : HoleStyle.SIMPLE, "endStyle" : HoleEndStyle.BLIND, "oppositeDirection" : true, "holeDiameter" : 3.3 * mm, "majorDiameter" : 5 * mm, "holeDepth" : 8 * mm, "isTappedThrough" : true, "tappedDepth" : 10.5 * mm, "tapClearance" : 3, "locations" : qUnion([Q0, Q1]), "scope" : qUnion([Q2, Q3])});
        }
        {
            var Q0;
            Q0=makeQuery(id+"F18.opExtrude","CAP_FACE",FACE,{"disambiguationData":[OSD([sQuery(id+"F17.wireOp",EDGE,"E22")])],"isStart":false});
            var sketch = newSketch(context, id + "F21", { "sketchPlane" : qUnion([Q0])});
            skPoint(sketch, "E76", {"position": v(-61.03, 1.98) * mm});
            skPoint(sketch, "E77", {"position": v(-53.03, -6.02) * mm});
            skPoint(sketch, "E78", {"position": v(-61.03, -14.02) * mm});
            skPoint(sketch, "E79", {"position": v(-69.03, -6.02) * mm});
            skPoint(sketch, "E80", {"position": v(-87.05, 34.73) * mm});
            skPoint(sketch, "E81", {"position": v(-103.05, 34.73) * mm});
            skPoint(sketch, "E82", {"position": v(-95.05, 42.73) * mm});
            skPoint(sketch, "E83", {"position": v(-95.05, 26.73) * mm});
            skSolve(sketch);
        }
        {
            var Q0;
            Q0=sQuery(id+"F21.wireOp",VERTEX,"E76");
            var Q1;
            Q1=sQuery(id+"F21.wireOp",VERTEX,"E77");
            var Q2;
            Q2=sQuery(id+"F21.wireOp",VERTEX,"E78");
            var Q3;
            Q3=sQuery(id+"F21.wireOp",VERTEX,"E79");
            var Q4;
            Q4=makeQuery(id+"F18.opExtrude","SWEPT_BODY",BODY,{"disambiguationData":[OSD([sQuery(id+"F17.wireOp",EDGE,"E22")])]});
            hole(context, id + "F22", {"style" : HoleStyle.C_BORE, "endStyle" : HoleEndStyle.BLIND, "holeDiameter" : 2.4 * mm, "cBoreDiameter" : 4 * mm, "cBoreDepth" : 2 * mm, "majorDiameter" : 5 * mm, "holeDepth" : 10 * mm, "isTappedThrough" : true, "tappedDepth" : 10.5 * mm, "tapClearance" : 3, "locations" : qUnion([Q0, Q1, Q2, Q3]), "scope" : qUnion([Q4])});
        }
        {
            var Q0;
            Q0=makeQuery(id+"F17.imprint","IMPRINT",FACE,{"disambiguationData":[TD([[makeQuery(id+"F17.imprint","IMPRINT",EDGE,{"derivedFrom":sQuery(id+"F17.wireOp",EDGE,"E29")}),1.0]])]});
            var Q1;
            Q1=makeQuery(id+"F17.imprint","IMPRINT",FACE,{"disambiguationData":[TD([[makeQuery(id+"F17.imprint","IMPRINT",EDGE,{"derivedFrom":sQuery(id+"F17.wireOp",EDGE,"E35.0")}),-1.0]])]});
            var Q2;
            Q2=makeQuery(id+"F17.imprint","IMPRINT",FACE,{"disambiguationData":[TD([[makeQuery(id+"F17.imprint","IMPRINT",EDGE,{"derivedFrom":sQuery(id+"F17.wireOp",EDGE,"E34.0")}),-1.0]])]});
            var Q3;
            Q3=makeQuery(id+"F17.imprint","IMPRINT",FACE,{"disambiguationData":[TD([[makeQuery(id+"F17.imprint","IMPRINT",EDGE,{"derivedFrom":sQuery(id+"F17.wireOp",EDGE,"E36.0")}),-1.0]])]});
            var Q4;
            Q4=makeQuery(id+"F17.imprint","IMPRINT",FACE,{"disambiguationData":[TD([[makeQuery(id+"F17.imprint","IMPRINT",EDGE,{"derivedFrom":sQuery(id+"F17.wireOp",EDGE,"E37.0")}),-1.0]])]});
            var Q5;
            Q5=makeQuery(id+"F17.imprint","IMPRINT",FACE,{"disambiguationData":[TD([[makeQuery(id+"F17.imprint","IMPRINT",EDGE,{"derivedFrom":sQuery(id+"F17.wireOp",EDGE,"E50")}),1.0]])]});
            var Q6;
            {var subQ1=sQuery(id+"F17.wireOp",EDGE,"E56.1");Q6=makeQuery(id+"F17.imprint","IMPRINT",FACE,{"disambiguationData":[TD([[makeQuery(id+"F17.imprint","IMPRINT",EDGE,{"derivedFrom":subQ1}),-1.0]])]});}
            var Q7;
            {var subQ4=sQuery(id+"F17.wireOp",EDGE,"2c43217e-bb20-4f4a-9b43-b0697576f654.1");Q7=makeQuery(id+"F17.imprint","IMPRINT",FACE,{"disambiguationData":[TD([[makeQuery(id+"F17.imprint","IMPRINT",EDGE,{"derivedFrom":subQ4}),-1.0]])]});}
            var Q8;
            {var subQ2=sQuery(id+"F17.wireOp",EDGE,"E55.0");Q8=makeQuery(id+"F17.imprint","IMPRINT",FACE,{"disambiguationData":[TD([[makeQuery(id+"F17.imprint","IMPRINT",EDGE,{"derivedFrom":subQ2}),-1.0]])]});}
            var Q9;
            {var subQ4=sQuery(id+"F17.wireOp",EDGE,"6faf811b-a0f7-47ac-b739-53598f2299f6.3");Q9=makeQuery(id+"F17.imprint","IMPRINT",FACE,{"disambiguationData":[TD([[makeQuery(id+"F17.imprint","IMPRINT",EDGE,{"derivedFrom":subQ4}),-1.0]])]});}
            var Q10;
            {var subQ1=sQuery(id+"F17.wireOp",EDGE,"E64.0");Q10=makeQuery(id+"F17.imprint","IMPRINT",FACE,{"disambiguationData":[TD([[makeQuery(id+"F17.imprint","IMPRINT",EDGE,{"derivedFrom":subQ1}),-1.0]])]});}
            var Q11;
            {var subQ6=sQuery(id+"F17.wireOp",EDGE,"E65.0");Q11=makeQuery(id+"F17.imprint","IMPRINT",FACE,{"disambiguationData":[TD([[makeQuery(id+"F17.imprint","IMPRINT",EDGE,{"derivedFrom":subQ6}),-1.0]])]});}
            extrude(context, id + "F23", {"entities" : qUnion([Q0, Q1, Q2, Q3, Q4, Q5, Q6, Q7, Q8, Q9, Q10, Q11]), "depth" : 3.5 * mm, "offsetDistance" : 25 * mm});
        }
        {
            var Q0;
            Q0=makeQuery(id+"F17.imprint","IMPRINT",FACE,{"disambiguationData":[TD([[makeQuery(id+"F17.imprint","IMPRINT",EDGE,{"derivedFrom":sQuery(id+"F17.wireOp",EDGE,"E34.0")}),-1.0]])]});
            var Q1;
            Q1=makeQuery(id+"F17.imprint","IMPRINT",FACE,{"disambiguationData":[TD([[makeQuery(id+"F17.imprint","IMPRINT",EDGE,{"derivedFrom":sQuery(id+"F17.wireOp",EDGE,"E35.0")}),-1.0]])]});
            var Q2;
            Q2=makeQuery(id+"F17.imprint","IMPRINT",FACE,{"disambiguationData":[TD([[makeQuery(id+"F17.imprint","IMPRINT",EDGE,{"derivedFrom":sQuery(id+"F17.wireOp",EDGE,"E36.0")}),-1.0]])]});
            var Q3;
            Q3=makeQuery(id+"F17.imprint","IMPRINT",FACE,{"disambiguationData":[TD([[makeQuery(id+"F17.imprint","IMPRINT",EDGE,{"derivedFrom":sQuery(id+"F17.wireOp",EDGE,"E37.0")}),-1.0]])]});
            var Q4;
            {var subQ4=sQuery(id+"F17.wireOp",EDGE,"6faf811b-a0f7-47ac-b739-53598f2299f6.3");Q4=makeQuery(id+"F17.imprint","IMPRINT",FACE,{"disambiguationData":[TD([[makeQuery(id+"F17.imprint","IMPRINT",EDGE,{"derivedFrom":subQ4}),-1.0]])]});}
            var Q5;
            {var subQ1=sQuery(id+"F17.wireOp",EDGE,"E56.1");Q5=makeQuery(id+"F17.imprint","IMPRINT",FACE,{"disambiguationData":[TD([[makeQuery(id+"F17.imprint","IMPRINT",EDGE,{"derivedFrom":subQ1}),-1.0]])]});}
            var Q6;
            {var subQ4=sQuery(id+"F17.wireOp",EDGE,"2c43217e-bb20-4f4a-9b43-b0697576f654.1");Q6=makeQuery(id+"F17.imprint","IMPRINT",FACE,{"disambiguationData":[TD([[makeQuery(id+"F17.imprint","IMPRINT",EDGE,{"derivedFrom":subQ4}),-1.0]])]});}
            var Q7;
            {var subQ2=sQuery(id+"F17.wireOp",EDGE,"E55.0");Q7=makeQuery(id+"F17.imprint","IMPRINT",FACE,{"disambiguationData":[TD([[makeQuery(id+"F17.imprint","IMPRINT",EDGE,{"derivedFrom":subQ2}),-1.0]])]});}
            var Q8;
            {var subQ1=sQuery(id+"F17.wireOp",EDGE,"E64.0");Q8=makeQuery(id+"F17.imprint","IMPRINT",FACE,{"disambiguationData":[TD([[makeQuery(id+"F17.imprint","IMPRINT",EDGE,{"derivedFrom":subQ1}),-1.0]])]});}
            var Q9;
            {var subQ6=sQuery(id+"F17.wireOp",EDGE,"E65.0");Q9=makeQuery(id+"F17.imprint","IMPRINT",FACE,{"disambiguationData":[TD([[makeQuery(id+"F17.imprint","IMPRINT",EDGE,{"derivedFrom":subQ6}),-1.0]])]});}
            extrude(context, id + "F24", {"entities" : qUnion([Q0, Q1, Q2, Q3, Q4, Q5, Q6, Q7, Q8, Q9]), "operationType" : NewBodyOperationType.REMOVE, "depth" : 1.5 * mm, "offsetDistance" : 25 * mm});
        }
        {
            var Q0;
            Q0=sQuery(id+"F17.wireOp",VERTEX,"E36.cCircle.center");
            var Q1;
            Q1=sQuery(id+"F17.wireOp",VERTEX,"E35.cCircle.center");
            var Q2;
            Q2=sQuery(id+"F17.wireOp",VERTEX,"E33");
            var Q3;
            Q3=sQuery(id+"F17.wireOp",VERTEX,"E32");
            var Q4;
            Q4=sQuery(id+"F17.wireOp",VERTEX,"E53");
            var Q5;
            Q5=sQuery(id+"F17.wireOp",VERTEX,"E54");
            var Q6;
            Q6=sQuery(id+"F17.wireOp",VERTEX,"E51");
            var Q7;
            Q7=sQuery(id+"F17.wireOp",VERTEX,"E52");
            var Q8;
            Q8=makeQuery(id+"F23.opExtrude","SWEPT_BODY",BODY,{"disambiguationData":[OSD([sQuery(id+"F17.wireOp",EDGE,"E29")])]});
            var Q9;
            Q9=makeQuery(id+"F23.opExtrude","SWEPT_BODY",BODY,{"disambiguationData":[OSD([sQuery(id+"F17.wireOp",EDGE,"E50"),sQuery(id+"F17.wireOp",EDGE,"E61")])]});
            hole(context, id + "F25", {"style" : HoleStyle.SIMPLE, "endStyle" : HoleEndStyle.BLIND, "oppositeDirection" : true, "holeDiameter" : 2.4 * mm, "majorDiameter" : 5 * mm, "holeDepth" : 10 * mm, "isTappedThrough" : true, "tappedDepth" : 10.5 * mm, "tapClearance" : 3, "locations" : qUnion([Q0, Q1, Q2, Q3, Q4, Q5, Q6, Q7]), "scope" : qUnion([Q8, Q9])});
        }
        {
            var Q0;
            {var subQ0=sQuery(id+"F17.wireOp",EDGE,"E48.bottom");Q0=makeQuery(id+"F17.imprint","IMPRINT",FACE,{"disambiguationData":[TD([[makeQuery(id+"F17.imprint","IMPRINT",EDGE,{"derivedFrom":subQ0}),-1.0]])]});}
            var Q1;
            {var subQ0=sQuery(id+"F17.wireOp",EDGE,"E48.top");Q1=makeQuery(id+"F17.imprint","IMPRINT",FACE,{"disambiguationData":[TD([[makeQuery(id+"F17.imprint","IMPRINT",EDGE,{"derivedFrom":subQ0}),1.0]])]});}
            var Q2;
            {var subQ0=sQuery(id+"F17.wireOp",EDGE,"E48.left");var subQ1=sQuery(id+"F17.wireOp",EDGE,"E42");var subQ2=makeQuery(id+"F17.imprint","INTERSECT",VERTEX,{"disambiguationData":[OD(0.0)],"derivedFrom":[subQ1,subQ0]});Q2=makeQuery(id+"F17.imprint","IMPRINT",FACE,{"disambiguationData":[TD([[makeQuery(id+"F17.imprint","IMPRINT",EDGE,{"disambiguationData":[TD([[subQ2,-1.0]])],"derivedFrom":subQ1}),-1.0]])]});}
            var Q3;
            {var subQ0=sQuery(id+"F17.wireOp",EDGE,"E48.right");var subQ1=sQuery(id+"F17.wireOp",EDGE,"E45");var subQ2=makeQuery(id+"F17.imprint","INTERSECT",VERTEX,{"disambiguationData":[OD(0.0)],"derivedFrom":[subQ1,subQ0]});Q3=makeQuery(id+"F17.imprint","IMPRINT",FACE,{"disambiguationData":[TD([[makeQuery(id+"F17.imprint","IMPRINT",EDGE,{"disambiguationData":[TD([[subQ2,1.0]])],"derivedFrom":subQ1}),-1.0]])]});}
            var Q4;
            {var subQ0=sQuery(id+"F17.wireOp",EDGE,"E46");var subQ1=sQuery(id+"F17.wireOp",EDGE,"E44");var subQ2=makeQuery(id+"F17.imprint","INTERSECT",VERTEX,{"derivedFrom":[subQ1,subQ0]});Q4=makeQuery(id+"F17.imprint","IMPRINT",FACE,{"disambiguationData":[TD([[makeQuery(id+"F17.imprint","IMPRINT",EDGE,{"disambiguationData":[TD([[subQ2,-1.0]])],"derivedFrom":subQ1}),1.0]])]});}
            var Q5;
            {var subQ0=sQuery(id+"F17.wireOp",EDGE,"E48.left");var subQ1=sQuery(id+"F17.wireOp",EDGE,"E42");var subQ2=makeQuery(id+"F17.imprint","INTERSECT",VERTEX,{"disambiguationData":[OD(0.0)],"derivedFrom":[subQ1,subQ0]});Q5=makeQuery(id+"F17.imprint","IMPRINT",FACE,{"disambiguationData":[TD([[makeQuery(id+"F17.imprint","IMPRINT",EDGE,{"disambiguationData":[TD([[subQ2,1.0]])],"derivedFrom":subQ1}),-1.0]])]});}
            var Q6;
            {var subQ0=sQuery(id+"F17.wireOp",EDGE,"E46");var subQ1=sQuery(id+"F17.wireOp",EDGE,"E44");var subQ2=makeQuery(id+"F17.imprint","INTERSECT",VERTEX,{"derivedFrom":[subQ1,subQ0]});Q6=makeQuery(id+"F17.imprint","IMPRINT",FACE,{"disambiguationData":[TD([[makeQuery(id+"F17.imprint","IMPRINT",EDGE,{"disambiguationData":[TD([[subQ2,-1.0]])],"derivedFrom":subQ1}),-1.0]])]});}
            var Q7;
            {var subQ0=sQuery(id+"F17.wireOp",EDGE,"E44");var subQ1=sQuery(id+"F17.wireOp",EDGE,"E42");var subQ2=makeQuery(id+"F17.imprint","INTERSECT",VERTEX,{"derivedFrom":[subQ1,subQ0]});Q7=makeQuery(id+"F17.imprint","IMPRINT",FACE,{"disambiguationData":[TD([[makeQuery(id+"F17.imprint","IMPRINT",EDGE,{"disambiguationData":[TD([[subQ2,1.0]])],"derivedFrom":subQ1}),-1.0]])]});}
            var Q8;
            {var subQ0=sQuery(id+"F17.wireOp",EDGE,"E48.left");var subQ1=sQuery(id+"F17.wireOp",EDGE,"E42");var subQ2=makeQuery(id+"F17.imprint","INTERSECT",VERTEX,{"disambiguationData":[OD(0.0)],"derivedFrom":[subQ1,subQ0]});Q8=makeQuery(id+"F17.imprint","IMPRINT",FACE,{"disambiguationData":[TD([[makeQuery(id+"F17.imprint","IMPRINT",EDGE,{"disambiguationData":[TD([[subQ2,-1.0]])],"derivedFrom":subQ1}),1.0]])]});}
            var Q9;
            {var subQ0=sQuery(id+"F17.wireOp",EDGE,"E48.right");var subQ1=sQuery(id+"F17.wireOp",EDGE,"E45");var subQ2=makeQuery(id+"F17.imprint","INTERSECT",VERTEX,{"disambiguationData":[OD(0.0)],"derivedFrom":[subQ1,subQ0]});Q9=makeQuery(id+"F17.imprint","IMPRINT",FACE,{"disambiguationData":[TD([[makeQuery(id+"F17.imprint","IMPRINT",EDGE,{"disambiguationData":[TD([[subQ2,1.0]])],"derivedFrom":subQ1}),1.0]])]});}
            var Q10;
            {var subQ0=sQuery(id+"F17.wireOp",EDGE,"E44");var subQ1=sQuery(id+"F17.wireOp",EDGE,"E42");var subQ2=makeQuery(id+"F17.imprint","INTERSECT",VERTEX,{"derivedFrom":[subQ1,subQ0]});Q10=makeQuery(id+"F17.imprint","IMPRINT",FACE,{"disambiguationData":[TD([[makeQuery(id+"F17.imprint","IMPRINT",EDGE,{"disambiguationData":[TD([[subQ2,1.0]])],"derivedFrom":subQ1}),1.0]])]});}
            var Q11;
            {var subQ0=sQuery(id+"F17.wireOp",EDGE,"E48.left");var subQ1=sQuery(id+"F17.wireOp",EDGE,"E42");var subQ2=makeQuery(id+"F17.imprint","INTERSECT",VERTEX,{"disambiguationData":[OD(0.0)],"derivedFrom":[subQ1,subQ0]});Q11=makeQuery(id+"F17.imprint","IMPRINT",FACE,{"disambiguationData":[TD([[makeQuery(id+"F17.imprint","IMPRINT",EDGE,{"disambiguationData":[TD([[subQ2,1.0]])],"derivedFrom":subQ1}),1.0]])]});}
            var Q12;
            {var subQ0=sQuery(id+"F17.wireOp",EDGE,"E48.right");var subQ1=sQuery(id+"F17.wireOp",EDGE,"E44");var subQ2=makeQuery(id+"F17.imprint","INTERSECT",VERTEX,{"derivedFrom":[subQ1,subQ0]});Q12=makeQuery(id+"F17.imprint","IMPRINT",FACE,{"disambiguationData":[TD([[makeQuery(id+"F17.imprint","IMPRINT",EDGE,{"disambiguationData":[TD([[subQ2,1.0]])],"derivedFrom":subQ1}),-1.0]])]});}
            var Q13;
            {var subQ0=sQuery(id+"F17.wireOp",EDGE,"E48.right");var subQ1=sQuery(id+"F17.wireOp",EDGE,"E44");var subQ2=makeQuery(id+"F17.imprint","INTERSECT",VERTEX,{"derivedFrom":[subQ1,subQ0]});Q13=makeQuery(id+"F17.imprint","IMPRINT",FACE,{"disambiguationData":[TD([[makeQuery(id+"F17.imprint","IMPRINT",EDGE,{"disambiguationData":[TD([[subQ2,1.0]])],"derivedFrom":subQ1}),1.0]])]});}
            var Q14;
            {var subQ0=sQuery(id+"F17.wireOp",EDGE,"E48.left");var subQ3=sQuery(id+"F17.wireOp",EDGE,"E44");var subQ5=makeQuery(id+"F17.imprint","INTERSECT",VERTEX,{"derivedFrom":[subQ3,subQ0]});Q14=makeQuery(id+"F17.imprint","IMPRINT",FACE,{"disambiguationData":[TD([[makeQuery(id+"F17.imprint","IMPRINT",EDGE,{"disambiguationData":[TD([[subQ5,-1.0]])],"derivedFrom":subQ3}),-1.0]])]});}
            var Q15;
            {var subQ0=sQuery(id+"F17.wireOp",EDGE,"E48.left");var subQ3=sQuery(id+"F17.wireOp",EDGE,"E44");var subQ5=makeQuery(id+"F17.imprint","INTERSECT",VERTEX,{"derivedFrom":[subQ3,subQ0]});Q15=makeQuery(id+"F17.imprint","IMPRINT",FACE,{"disambiguationData":[TD([[makeQuery(id+"F17.imprint","IMPRINT",EDGE,{"disambiguationData":[TD([[subQ5,-1.0]])],"derivedFrom":subQ3}),1.0]])]});}
            extrude(context, id + "F26", {"entities" : qUnion([Q0, Q1, Q2, Q3, Q4, Q5, Q6, Q7, Q8, Q9, Q10, Q11, Q12, Q13, Q14, Q15]), "depth" : 5 * mm, "offsetDistance" : 25 * mm});
        }
        {
            var Q0;
            Q0=sQuery(id+"F17.wireOp",VERTEX,"E44.start");
            var Q1;
            Q1=sQuery(id+"F17.wireOp",VERTEX,"E44.end");
            var Q2;
            Q2=makeQuery(id+"F26.opExtrude","SWEPT_BODY",BODY,{"disambiguationData":[OSD([sQuery(id+"F17.wireOp",EDGE,"E42"),sQuery(id+"F17.wireOp",EDGE,"E43"),sQuery(id+"F17.wireOp",EDGE,"E45"),sQuery(id+"F17.wireOp",EDGE,"E46"),sQuery(id+"F17.wireOp",EDGE,"E48.bottom"),sQuery(id+"F17.wireOp",EDGE,"E48.top"),sQuery(id+"F17.wireOp",EDGE,"E48.left"),sQuery(id+"F17.wireOp",EDGE,"E48.right")])]});
            hole(context, id + "F27", {"style" : HoleStyle.SIMPLE, "endStyle" : HoleEndStyle.BLIND, "oppositeDirection" : true, "holeDiameter" : 3.7 * mm, "majorDiameter" : 5 * mm, "holeDepth" : 10 * mm, "isTappedThrough" : true, "tappedDepth" : 10.5 * mm, "tapClearance" : 3, "locations" : qUnion([Q0, Q1]), "scope" : qUnion([Q2])});
        }
        {
            var Q0;
            {var subQ0=sQuery(id+"F17.wireOp",EDGE,"E48.right");var subQ1=sQuery(id+"F17.wireOp",EDGE,"E45");var subQ2=makeQuery(id+"F17.imprint","INTERSECT",VERTEX,{"disambiguationData":[OD(0.0)],"derivedFrom":[subQ1,subQ0]});Q0=makeQuery(id+"F17.imprint","IMPRINT",FACE,{"disambiguationData":[TD([[makeQuery(id+"F17.imprint","IMPRINT",EDGE,{"disambiguationData":[TD([[subQ2,1.0]])],"derivedFrom":subQ1}),1.0]])]});}
            var Q1;
            {var subQ0=sQuery(id+"F17.wireOp",EDGE,"E48.left");var subQ1=sQuery(id+"F17.wireOp",EDGE,"E42");var subQ2=makeQuery(id+"F17.imprint","INTERSECT",VERTEX,{"disambiguationData":[OD(0.0)],"derivedFrom":[subQ1,subQ0]});Q1=makeQuery(id+"F17.imprint","IMPRINT",FACE,{"disambiguationData":[TD([[makeQuery(id+"F17.imprint","IMPRINT",EDGE,{"disambiguationData":[TD([[subQ2,-1.0]])],"derivedFrom":subQ1}),1.0]])]});}
            extrude(context, id + "F28", {"entities" : qUnion([Q0, Q1]), "operationType" : NewBodyOperationType.REMOVE, "depth" : 5 * mm, "offsetDistance" : 25 * mm});
        }
        {
            var Q0;
            Q0=makeQuery(id+"F26.opExtrude","CAP_EDGE",EDGE,{"disambiguationData":[OSD([sQuery(id+"F17.wireOp",EDGE,"E43")])],"isStart":false});
            var Q1;
            Q1=makeQuery(id+"F26.opExtrude","CAP_EDGE",EDGE,{"disambiguationData":[OSD([sQuery(id+"F17.wireOp",EDGE,"E48.top")])],"isStart":false});
            var Q2;
            Q2=makeQuery(id+"F26.opExtrude","CAP_EDGE",EDGE,{"disambiguationData":[OSD([sQuery(id+"F17.wireOp",EDGE,"E48.bottom")])],"isStart":false});
            var Q3;
            Q3=makeQuery(id+"F26.opExtrude","CAP_EDGE",EDGE,{"disambiguationData":[OSD([sQuery(id+"F17.wireOp",EDGE,"E46")])],"isStart":false});
            var Q4;
            Q4=makeQuery(id+"F26.opExtrude","CAP_EDGE",EDGE,{"disambiguationData":[OSD([sQuery(id+"F17.wireOp",EDGE,"E43")])],"isStart":true});
            var Q5;
            Q5=makeQuery(id+"F26.opExtrude","CAP_EDGE",EDGE,{"disambiguationData":[OSD([sQuery(id+"F17.wireOp",EDGE,"E48.top")])],"isStart":true});
            var Q6;
            Q6=makeQuery(id+"F26.opExtrude","CAP_EDGE",EDGE,{"disambiguationData":[OSD([sQuery(id+"F17.wireOp",EDGE,"E48.bottom")])],"isStart":true});
            var Q7;
            Q7=makeQuery(id+"F26.opExtrude","CAP_EDGE",EDGE,{"disambiguationData":[OSD([sQuery(id+"F17.wireOp",EDGE,"E46")])],"isStart":true});
            fillet(context, id + "F29", {"entities" : qUnion([Q0, Q1, Q2, Q3, Q4, Q5, Q6, Q7]), "radius" : 2 * mm, "tangentPropagation" : true, "allowEdgeOverflow" : false});
        }
        {
            var Q0;
            Q0=makeQuery(id+"F17.imprint","IMPRINT",FACE,{"disambiguationData":[TD([[makeQuery(id+"F17.imprint","IMPRINT",EDGE,{"derivedFrom":sQuery(id+"F17.wireOp",EDGE,"E72.0")}),1.0]])]});
            extrude(context, id + "F30", {"entities" : qUnion([Q0]), "operationType" : NewBodyOperationType.REMOVE, "depth" : 2 * mm, "offsetDistance" : 25 * mm});
        }
        {
            var Q0;
            Q0=sQuery(id+"F21.wireOp",VERTEX,"E80");
            var Q1;
            Q1=sQuery(id+"F21.wireOp",VERTEX,"E82");
            var Q2;
            Q2=sQuery(id+"F21.wireOp",VERTEX,"E81");
            var Q3;
            Q3=sQuery(id+"F21.wireOp",VERTEX,"E83");
            var Q4;
            Q4=makeQuery(id+"F18.opExtrude","SWEPT_BODY",BODY,{"disambiguationData":[OSD([sQuery(id+"F17.wireOp",EDGE,"E67")])]});
            hole(context, id + "F31", {"style" : HoleStyle.C_BORE, "endStyle" : HoleEndStyle.BLIND, "holeDiameter" : 2.4 * mm, "cBoreDiameter" : 4 * mm, "cBoreDepth" : 0.6 * mm, "majorDiameter" : 5 * mm, "holeDepth" : 8 * mm, "isTappedThrough" : true, "tappedDepth" : 10.5 * mm, "tapClearance" : 3, "locations" : qUnion([Q0, Q1, Q2, Q3]), "scope" : qUnion([Q4])});
        }
    });
